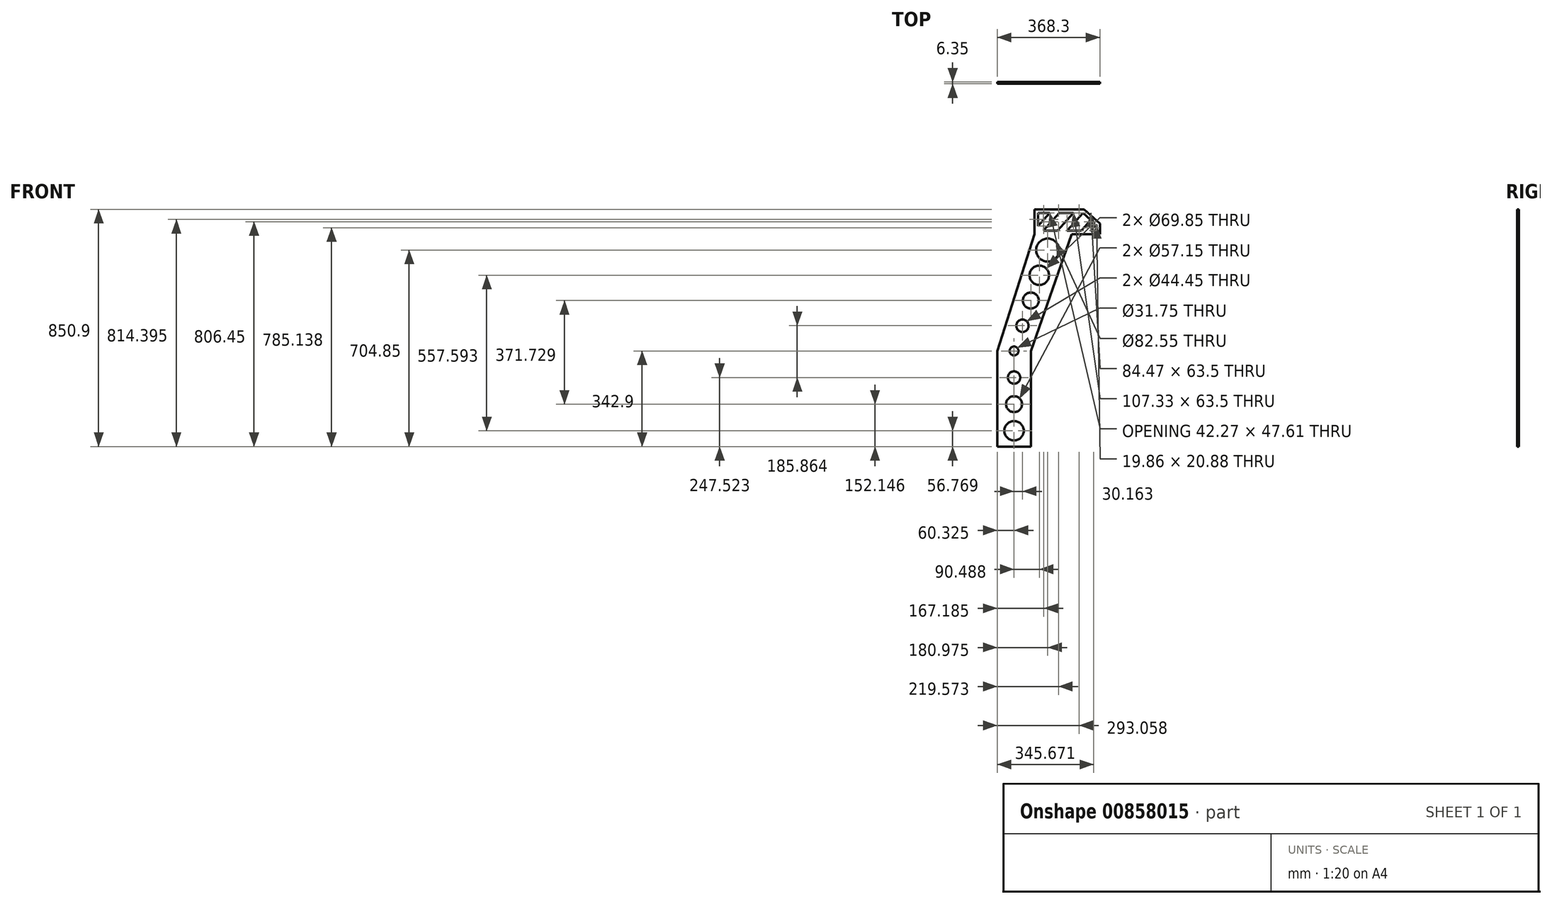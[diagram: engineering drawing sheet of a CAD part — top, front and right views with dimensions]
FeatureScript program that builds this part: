
annotation { "Feature Type Name" : "Feature", "Feature Type Description" : "" }
export const myFeature = defineFeature(function(context is Context, id is Id, definition is map)
    precondition{}
    {
        {
            var Q0;
            Q0=qCreatedBy(makeId("Front.planeOp"),FACE);
            var sketch = newSketch(context, id + "F0", { "sketchPlane" : qUnion([Q0])});
            skLineSegment(sketch, "E0", {"start": v(0, 0) * mm, "end": v(0, 850.9) * mm, "construction": true});
            skLineSegment(sketch, "E1", {"start": v(0, 850.9) * mm, "end": v(152.4, 850.9) * mm, "construction": true});
            skLineSegment(sketch, "E2", {"start": v(152.4, 850.9) * mm, "end": v(152.4, 762) * mm, "construction": true});
            skLineSegment(sketch, "E3", {"start": v(152.4, 762) * mm, "end": v(0, 762) * mm, "construction": true});
            skLineSegment(sketch, "E4", {"start": v(0, 0) * mm, "end": v(-120.65, 0) * mm, "construction": true});
            skLineSegment(sketch, "E5", {"start": v(-120.65, 0) * mm, "end": v(-120.65, 847.12) * mm, "construction": true});
            skLineSegment(sketch, "E6", {"start": v(-60.33, 0) * mm, "end": v(-60.33, 342.9) * mm, "construction": true});
            skLineSegment(sketch, "E7", {"start": v(152.4, 762) * mm, "end": v(247.65, 762) * mm, "construction": true});
            skLineSegment(sketch, "E8", {"start": v(-120.65, 0) * mm, "end": v(0, 0) * mm});
            skLineSegment(sketch, "E9", {"start": v(0, 342.9) * mm, "end": v(0, 0) * mm});
            skLineSegment(sketch, "E10", {"start": v(-120.65, 0) * mm, "end": v(-120.65, 342.9) * mm});
            skLineSegment(sketch, "E11", {"start": v(0, 342.9) * mm, "end": v(146.05, 762) * mm});
            skLineSegment(sketch, "E12", {"start": v(146.05, 762) * mm, "end": v(12.7, 762) * mm});
            skLineSegment(sketch, "E13", {"start": v(12.7, 762) * mm, "end": v(-120.65, 342.9) * mm});
            skLineSegment(sketch, "E14", {"start": v(12.7, 762) * mm, "end": v(12.7, 850.9) * mm});
            skLineSegment(sketch, "E15", {"start": v(12.7, 850.9) * mm, "end": v(247.65, 850.9) * mm});
            skLineSegment(sketch, "E16", {"start": v(247.65, 850.9) * mm, "end": v(247.65, 762) * mm});
            skLineSegment(sketch, "E17", {"start": v(146.05, 762) * mm, "end": v(247.65, 762) * mm});
            skSolve(sketch);
        }
        {
            var Q0;
            Q0 = qSketchRegion(id + "F0", true);
            extrude(context, id + "F1", {"entities" : qUnion([Q0]), "depth" : 6.35 * mm, "offsetDistance" : 25.4 * mm});
        }
        {
            var Q0;
            Q0=makeQuery(id+"F1.opExtrude","CAP_FACE",FACE,{"disambiguationData":[OSD([sQuery(id+"F0.wireOp",EDGE,"E8"),sQuery(id+"F0.wireOp",EDGE,"E9"),sQuery(id+"F0.wireOp",EDGE,"E10"),sQuery(id+"F0.wireOp",EDGE,"E11"),sQuery(id+"F0.wireOp",EDGE,"E13"),sQuery(id+"F0.wireOp",EDGE,"E14"),sQuery(id+"F0.wireOp",EDGE,"E15"),sQuery(id+"F0.wireOp",EDGE,"E16"),sQuery(id+"F0.wireOp",EDGE,"E17")])],"isStart":false});
            var sketch = newSketch(context, id + "F2", { "sketchPlane" : qUnion([Q0])});
            skLineSegment(sketch, "E18", {"start": v(190.5, 850.9) * mm, "end": v(247.65, 800.1) * mm});
            skLineSegment(sketch, "E19", {"start": v(247.65, 800.1) * mm, "end": v(247.65, 850.9) * mm});
            skLineSegment(sketch, "E20", {"start": v(247.65, 850.9) * mm, "end": v(190.5, 850.9) * mm});
            skSolve(sketch);
        }
        {
            var Q0;
            Q0=makeQuery(id+"F2.imprint","IMPRINT",FACE,{"disambiguationData":[TD([[makeQuery(id+"F2.imprint","IMPRINT",EDGE,{"derivedFrom":sQuery(id+"F2.wireOp",EDGE,"E18")}),1.0]])]});
            extrude(context, id + "F3", {"entities" : qUnion([Q0]), "operationType" : NewBodyOperationType.REMOVE, "oppositeDirection" : true, "depth" : 25.4 * mm, "offsetDistance" : 25.4 * mm});
        }
        {
            var Q0;
            Q0=makeQuery(id+"F1.opExtrude","CAP_FACE",FACE,{"disambiguationData":[OSD([sQuery(id+"F0.wireOp",EDGE,"E8"),sQuery(id+"F0.wireOp",EDGE,"E9"),sQuery(id+"F0.wireOp",EDGE,"E10"),sQuery(id+"F0.wireOp",EDGE,"E11"),sQuery(id+"F0.wireOp",EDGE,"E13"),sQuery(id+"F0.wireOp",EDGE,"E14"),sQuery(id+"F0.wireOp",EDGE,"E15"),sQuery(id+"F0.wireOp",EDGE,"E16"),sQuery(id+"F0.wireOp",EDGE,"E17")])],"isStart":false});
            var sketch = newSketch(context, id + "F4", { "sketchPlane" : qUnion([Q0])});
            skLineSegment(sketch, "E21.bottom", {"start": v(25.4, 838.2) * mm, "end": v(185.67, 838.2) * mm});
            skLineSegment(sketch, "E21.left", {"start": v(25.4, 838.2) * mm, "end": v(25.4, 774.7) * mm});
            skLineSegment(sketch, "E22", {"start": v(185.67, 838.2) * mm, "end": v(234.95, 794.4) * mm});
            skLineSegment(sketch, "E23", {"start": v(234.95, 794.4) * mm, "end": v(234.95, 774.7) * mm});
            skLineSegment(sketch, "E24", {"start": v(25.4, 774.7) * mm, "end": v(234.95, 774.7) * mm});
            skCircle(sketch, "E25", {"center": v(-60.33, 342.9) * mm, "radius": 15.88 * mm});
            skCircle(sketch, "E26", {"center": v(-30.16, 433.39) * mm, "radius": 22.23 * mm});
            skCircle(sketch, "E27", {"center": v(0, 523.88) * mm, "radius": 28.58 * mm});
            skCircle(sketch, "E28", {"center": v(60.32, 704.85) * mm, "radius": 41.28 * mm});
            skCircle(sketch, "E29", {"center": v(30.16, 614.36) * mm, "radius": 34.93 * mm});
            skLineSegment(sketch, "E30", {"start": v(-120.65, 342.9) * mm, "end": v(0, 342.9) * mm, "construction": true});
            skLineSegment(sketch, "E31", {"start": v(0, 342.9) * mm, "end": v(12.7, 762) * mm, "construction": true});
            skLineSegment(sketch, "E32", {"start": v(12.7, 762) * mm, "end": v(146.05, 762) * mm, "construction": true});
            skLineSegment(sketch, "E33", {"start": v(79.38, 762) * mm, "end": v(-60.33, 342.9) * mm, "construction": true});
            skLineSegment(sketch, "E34", {"start": v(60.32, 704.85) * mm, "end": v(30.16, 614.36) * mm, "construction": true});
            skLineSegment(sketch, "E35", {"start": v(0, 523.88) * mm, "end": v(30.16, 614.36) * mm, "construction": true});
            skLineSegment(sketch, "E36", {"start": v(-30.16, 433.39) * mm, "end": v(0, 523.88) * mm, "construction": true});
            skLineSegment(sketch, "E37", {"start": v(-60.32, 342.9) * mm, "end": v(-30.16, 433.39) * mm, "construction": true});
            skLineSegment(sketch, "E38", {"start": v(101.64, 838.2) * mm, "end": v(45.26, 774.7) * mm});
            skLineSegment(sketch, "E39", {"start": v(96.2, 774.7) * mm, "end": v(152.59, 838.2) * mm});
            skLineSegment(sketch, "E40", {"start": v(186.55, 838.2) * mm, "end": v(130.17, 774.7) * mm});
            skLineSegment(sketch, "E41", {"start": v(214.64, 812.45) * mm, "end": v(181.12, 774.7) * mm});
            skLineSegment(sketch, "E42", {"start": v(25.4, 790.59) * mm, "end": v(67.67, 838.2) * mm});
            skLineSegment(sketch, "E43", {"start": v(215.1, 774.7) * mm, "end": v(233.62, 795.57) * mm});
            skLineSegment(sketch, "E44", {"start": v(25.4, 790.59) * mm, "end": v(25.4, 838.2) * mm});
            skLineSegment(sketch, "E45", {"start": v(25.4, 838.2) * mm, "end": v(67.67, 838.2) * mm});
            skLineSegment(sketch, "E46", {"start": v(101.64, 838.2) * mm, "end": v(152.59, 838.2) * mm});
            skLineSegment(sketch, "E47", {"start": v(45.26, 774.7) * mm, "end": v(96.2, 774.7) * mm});
            skLineSegment(sketch, "E48", {"start": v(130.17, 774.7) * mm, "end": v(181.12, 774.7) * mm});
            skLineSegment(sketch, "E49", {"start": v(186.55, 838.2) * mm, "end": v(214.64, 812.45) * mm});
            skLineSegment(sketch, "E50", {"start": v(233.62, 795.57) * mm, "end": v(234.95, 794.4) * mm});
            skLineSegment(sketch, "E51", {"start": v(-60.33, 342.9) * mm, "end": v(-60.33, 49.35) * mm, "construction": true});
            skCircle(sketch, "E52", {"center": v(-60.32, 247.52) * mm, "radius": 22.23 * mm});
            skCircle(sketch, "E53", {"center": v(-60.32, 152.15) * mm, "radius": 28.58 * mm});
            skCircle(sketch, "E54", {"center": v(-60.32, 56.77) * mm, "radius": 34.93 * mm});
            skSolve(sketch);
        }
        {
            var Q0;
            Q0=makeQuery(id+"F4.imprint","IMPRINT",FACE,{"disambiguationData":[TD([[makeQuery(id+"F4.imprint","IMPRINT",EDGE,{"derivedFrom":sQuery(id+"F4.wireOp",EDGE,"E25")}),1.0]])]});
            var Q1;
            Q1=makeQuery(id+"F4.imprint","IMPRINT",FACE,{"disambiguationData":[TD([[makeQuery(id+"F4.imprint","IMPRINT",EDGE,{"derivedFrom":sQuery(id+"F4.wireOp",EDGE,"E26")}),1.0]])]});
            var Q2;
            Q2=makeQuery(id+"F4.imprint","IMPRINT",FACE,{"disambiguationData":[TD([[makeQuery(id+"F4.imprint","IMPRINT",EDGE,{"derivedFrom":sQuery(id+"F4.wireOp",EDGE,"E28")}),1.0]])]});
            var Q3;
            {var subQ0=sQuery(id+"F4.wireOp",EDGE,"E49");Q3=makeQuery(id+"F4.imprint","IMPRINT",FACE,{"disambiguationData":[TD([[makeQuery(id+"F4.imprint","IMPRINT",EDGE,{"derivedFrom":subQ0}),-1.0]])]});}
            var Q4;
            {var subQ2=sQuery(id+"F4.wireOp",EDGE,"E43");Q4=makeQuery(id+"F4.imprint","IMPRINT",FACE,{"disambiguationData":[TD([[makeQuery(id+"F4.imprint","IMPRINT",EDGE,{"derivedFrom":subQ2}),-1.0]])]});}
            var Q5;
            {var subQ0=sQuery(id+"F4.wireOp",EDGE,"E31");var subQ1=sQuery(id+"F4.wireOp",EDGE,"E27");var subQ2=makeQuery(id+"F4.imprint","INTERSECT",VERTEX,{"disambiguationData":[OD(0.0)],"derivedFrom":[subQ1,subQ0]});Q5=makeQuery(id+"F4.imprint","IMPRINT",FACE,{"disambiguationData":[TD([[makeQuery(id+"F4.imprint","IMPRINT",EDGE,{"disambiguationData":[TD([[subQ2,1.0]])],"derivedFrom":subQ1}),1.0]])]});}
            var Q6;
            {var subQ0=sQuery(id+"F4.wireOp",EDGE,"E31");var subQ1=sQuery(id+"F4.wireOp",EDGE,"E27");var subQ2=makeQuery(id+"F4.imprint","INTERSECT",VERTEX,{"disambiguationData":[OD(0.0)],"derivedFrom":[subQ1,subQ0]});Q6=makeQuery(id+"F4.imprint","IMPRINT",FACE,{"disambiguationData":[TD([[makeQuery(id+"F4.imprint","IMPRINT",EDGE,{"disambiguationData":[TD([[subQ2,-1.0]])],"derivedFrom":subQ1}),1.0]])]});}
            var Q7;
            {var subQ0=sQuery(id+"F4.wireOp",EDGE,"E31");var subQ1=sQuery(id+"F4.wireOp",EDGE,"E29");var subQ2=makeQuery(id+"F4.imprint","INTERSECT",VERTEX,{"disambiguationData":[OD(0.0)],"derivedFrom":[subQ1,subQ0]});Q7=makeQuery(id+"F4.imprint","IMPRINT",FACE,{"disambiguationData":[TD([[makeQuery(id+"F4.imprint","IMPRINT",EDGE,{"disambiguationData":[TD([[subQ2,1.0]])],"derivedFrom":subQ1}),1.0]])]});}
            var Q8;
            Q8=makeQuery(id+"F4.imprint","IMPRINT",FACE,{"disambiguationData":[TD([[makeQuery(id+"F4.imprint","IMPRINT",EDGE,{"derivedFrom":sQuery(id+"F4.wireOp",EDGE,"E42")}),1.0]])]});
            var Q9;
            Q9=makeQuery(id+"F4.imprint","IMPRINT",FACE,{"disambiguationData":[TD([[makeQuery(id+"F4.imprint","IMPRINT",EDGE,{"derivedFrom":sQuery(id+"F4.wireOp",EDGE,"E38")}),1.0]])]});
            var Q10;
            {var subQ0=sQuery(id+"F4.wireOp",EDGE,"E41");Q10=makeQuery(id+"F4.imprint","IMPRINT",FACE,{"disambiguationData":[TD([[makeQuery(id+"F4.imprint","IMPRINT",EDGE,{"derivedFrom":subQ0}),-1.0]])]});}
            var Q11;
            {var subQ0=sQuery(id+"F4.wireOp",EDGE,"E31");var subQ1=sQuery(id+"F4.wireOp",EDGE,"E29");var subQ2=makeQuery(id+"F4.imprint","INTERSECT",VERTEX,{"disambiguationData":[OD(0.0)],"derivedFrom":[subQ1,subQ0]});Q11=makeQuery(id+"F4.imprint","IMPRINT",FACE,{"disambiguationData":[TD([[makeQuery(id+"F4.imprint","IMPRINT",EDGE,{"disambiguationData":[TD([[subQ2,-1.0]])],"derivedFrom":subQ1}),1.0]])]});}
            var Q12;
            Q12=makeQuery(id+"F4.imprint","IMPRINT",FACE,{"disambiguationData":[TD([[makeQuery(id+"F4.imprint","IMPRINT",EDGE,{"derivedFrom":sQuery(id+"F4.wireOp",EDGE,"E52")}),1.0]])]});
            var Q13;
            Q13=makeQuery(id+"F4.imprint","IMPRINT",FACE,{"disambiguationData":[TD([[makeQuery(id+"F4.imprint","IMPRINT",EDGE,{"derivedFrom":sQuery(id+"F4.wireOp",EDGE,"E53")}),1.0]])]});
            var Q14;
            Q14=makeQuery(id+"F4.imprint","IMPRINT",FACE,{"disambiguationData":[TD([[makeQuery(id+"F4.imprint","IMPRINT",EDGE,{"derivedFrom":sQuery(id+"F4.wireOp",EDGE,"E54")}),1.0]])]});
            extrude(context, id + "F5", {"entities" : qUnion([Q0, Q1, Q2, Q3, Q4, Q5, Q6, Q7, Q8, Q9, Q10, Q11, Q12, Q13, Q14]), "operationType" : NewBodyOperationType.REMOVE, "oppositeDirection" : true, "depth" : 25.4 * mm, "offsetDistance" : 25.4 * mm});
        }
    });
